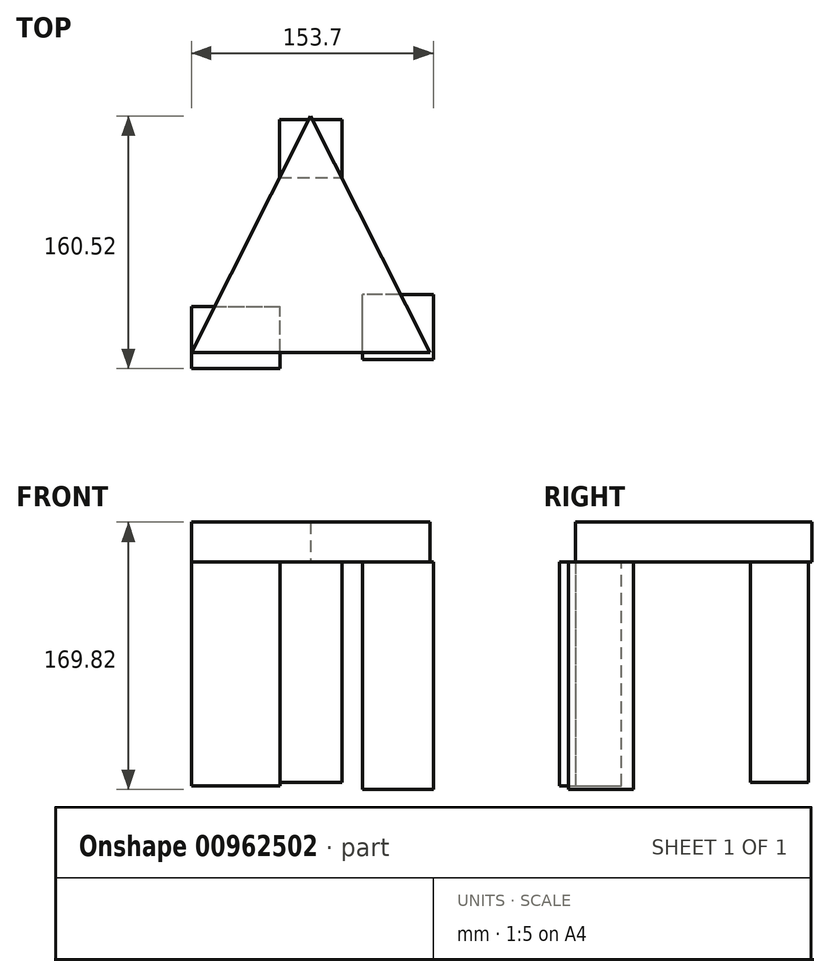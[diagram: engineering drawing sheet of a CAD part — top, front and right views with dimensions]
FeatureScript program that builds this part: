
annotation { "Feature Type Name" : "Feature", "Feature Type Description" : "" }
export const myFeature = defineFeature(function(context is Context, id is Id, definition is map)
    precondition{}
    {
        {
            var Q0;
            Q0=qCreatedBy(makeId("Top.planeOp"),FACE);
            var sketch = newSketch(context, id + "F0", { "sketchPlane" : qUnion([Q0])});
            skLineSegment(sketch, "E0", {"start": v(-13.9, 48.54) * mm, "end": v(-75.72, -75.51) * mm});
            skLineSegment(sketch, "E1", {"start": v(-75.72, -75.51) * mm, "end": v(0, 74.9) * mm});
            skLineSegment(sketch, "E2", {"start": v(75.72, -75.3) * mm, "end": v(0, 74.9) * mm});
            skLineSegment(sketch, "E3", {"start": v(75.72, -75.3) * mm, "end": v(-75.72, -75.51) * mm});
            skSolve(sketch);
        }
        {
            var Q0;
            Q0=makeQuery(id+"F0.imprint","IMPRINT",FACE,{"disambiguationData":[TD([[makeQuery(id+"F0.imprint","IMPRINT",EDGE,{"derivedFrom":sQuery(id+"F0.wireOp",EDGE,"E1")}),-1.0]])]});
            extrude(context, id + "F1", {"entities" : qUnion([Q0]), "depth" : 25.4 * mm, "offsetDistance" : 25.4 * mm});
        }
        {
            var Q0;
            Q0=makeQuery(id+"F1.opExtrude","CAP_FACE",FACE,{"disambiguationData":[OSD([sQuery(id+"F0.wireOp",EDGE,"E1"),sQuery(id+"F0.wireOp",EDGE,"E2"),sQuery(id+"F0.wireOp",EDGE,"E3")])],"isStart":true});
            var sketch = newSketch(context, id + "F2", { "sketchPlane" : qUnion([Q0])});
            skLineSegment(sketch, "E4.bottom", {"start": v(75.72, 75.3) * mm, "end": v(32.4, 75.3) * mm});
            skLineSegment(sketch, "E4.top", {"start": v(75.72, 43.67) * mm, "end": v(32.4, 43.67) * mm});
            skLineSegment(sketch, "E4.left", {"start": v(75.72, 75.3) * mm, "end": v(75.72, 43.67) * mm});
            skLineSegment(sketch, "E4.right", {"start": v(32.4, 75.3) * mm, "end": v(32.4, 43.67) * mm});
            skPoint(sketch, "E4.middle", {"position": v(54.06, 59.49) * mm});
            skLineSegment(sketch, "E5.bottom", {"start": v(-23.54, -28.13) * mm, "end": v(23.54, -28.13) * mm});
            skLineSegment(sketch, "E5.top", {"start": v(-23.54, -69.7) * mm, "end": v(23.54, -69.7) * mm});
            skLineSegment(sketch, "E5.left", {"start": v(-23.54, -28.13) * mm, "end": v(-23.54, -69.7) * mm});
            skLineSegment(sketch, "E5.right", {"start": v(23.54, -28.13) * mm, "end": v(23.54, -69.7) * mm});
            skPoint(sketch, "E5.middle", {"position": v(0, -48.92) * mm});
            skLineSegment(sketch, "E6.bottom", {"start": v(-85.45, 87) * mm, "end": v(-41.1, 87) * mm});
            skLineSegment(sketch, "E6.top", {"start": v(-85.45, 48.67) * mm, "end": v(-41.1, 48.67) * mm});
            skLineSegment(sketch, "E6.left", {"start": v(-85.45, 87) * mm, "end": v(-85.45, 48.67) * mm});
            skLineSegment(sketch, "E6.right", {"start": v(-41.1, 87) * mm, "end": v(-41.1, 48.67) * mm});
            skPoint(sketch, "E6.middle", {"position": v(-63.27, 67.84) * mm});
            skSolve(sketch);
        }
        {
            var Q0;
            Q0=makeQuery(id+"F1.opExtrude","CAP_FACE",FACE,{"disambiguationData":[OSD([sQuery(id+"F0.wireOp",EDGE,"E1"),sQuery(id+"F0.wireOp",EDGE,"E2"),sQuery(id+"F0.wireOp",EDGE,"E3")])],"isStart":true});
            var sketch = newSketch(context, id + "F3", { "sketchPlane" : qUnion([Q0])});
            skLineSegment(sketch, "E7.bottom", {"start": v(89.03, 89.1) * mm, "end": v(31.32, 89.1) * mm});
            skLineSegment(sketch, "E7.top", {"start": v(89.03, 31.83) * mm, "end": v(31.32, 31.83) * mm});
            skLineSegment(sketch, "E7.left", {"start": v(89.03, 89.1) * mm, "end": v(89.03, 31.83) * mm});
            skLineSegment(sketch, "E7.right", {"start": v(31.32, 89.1) * mm, "end": v(31.32, 31.83) * mm});
            skPoint(sketch, "E7.middle", {"position": v(60.17, 60.47) * mm});
            skSolve(sketch);
        }
        {
            var Q0;
            {var subQ0=sQuery(id+"F2.wireOp",EDGE,"E6.right");var subQ1=sQuery(id+"F2.wireOp",EDGE,"E6.top");var subQ2=makeQuery(id+"F2.imprint","INTERSECT",VERTEX,{"derivedFrom":[subQ1,subQ0]});Q0=makeQuery(id+"F2.imprint","IMPRINT",FACE,{"disambiguationData":[TD([[makeQuery(id+"F2.imprint","IMPRINT",EDGE,{"disambiguationData":[TD([[subQ2,1.0]])],"derivedFrom":subQ1}),1.0]])]});}
            var sketch = newSketch(context, id + "F4", { "sketchPlane" : qUnion([Q0])});
            skLineSegment(sketch, "E8.bottom", {"start": v(-75.55, 85.63) * mm, "end": v(-19.56, 85.63) * mm});
            skLineSegment(sketch, "E8.top", {"start": v(-75.55, 46.26) * mm, "end": v(-19.56, 46.26) * mm});
            skLineSegment(sketch, "E8.left", {"start": v(-75.55, 85.63) * mm, "end": v(-75.55, 46.26) * mm});
            skLineSegment(sketch, "E8.right", {"start": v(-19.56, 85.63) * mm, "end": v(-19.56, 46.26) * mm});
            skPoint(sketch, "E8.middle", {"position": v(-47.56, 65.95) * mm});
            skSolve(sketch);
        }
        {
            var Q0;
            {var subQ0=sQuery(id+"F2.wireOp",EDGE,"E6.right");var subQ1=sQuery(id+"F2.wireOp",EDGE,"E6.top");var subQ2=makeQuery(id+"F2.imprint","INTERSECT",VERTEX,{"derivedFrom":[subQ1,subQ0]});Q0=makeQuery(id+"F2.imprint","IMPRINT",FACE,{"disambiguationData":[TD([[makeQuery(id+"F2.imprint","IMPRINT",EDGE,{"disambiguationData":[TD([[subQ2,1.0]])],"derivedFrom":subQ1}),1.0]])]});}
            var Q1;
            Q1 = qSketchRegion(id + "F4", true);
            extrude(context, id + "F5", {"entities" : qUnion([Q0, Q1]), "operationType" : NewBodyOperationType.ADD, "depth" : 142.07 * mm, "offsetDistance" : 25.4 * mm});
        }
        {
            var Q0;
            Q0=makeQuery(id+"F1.opExtrude","CAP_FACE",FACE,{"disambiguationData":[OSD([sQuery(id+"F0.wireOp",EDGE,"E1"),sQuery(id+"F0.wireOp",EDGE,"E2"),sQuery(id+"F0.wireOp",EDGE,"E3")])],"isStart":true});
            var sketch = newSketch(context, id + "F6", { "sketchPlane" : qUnion([Q0])});
            skLineSegment(sketch, "E9.bottom", {"start": v(-19.84, -72.44) * mm, "end": v(19.84, -72.44) * mm});
            skLineSegment(sketch, "E9.top", {"start": v(-19.84, -35.89) * mm, "end": v(19.84, -35.89) * mm});
            skLineSegment(sketch, "E9.left", {"start": v(-19.84, -72.44) * mm, "end": v(-19.84, -35.89) * mm});
            skLineSegment(sketch, "E9.right", {"start": v(19.84, -72.44) * mm, "end": v(19.84, -35.89) * mm});
            skPoint(sketch, "E9.middle", {"position": v(0, -54.17) * mm});
            skSolve(sketch);
        }
        {
            var Q0;
            Q0 = qSketchRegion(id + "F6", true);
            extrude(context, id + "F7", {"entities" : qUnion([Q0]), "operationType" : NewBodyOperationType.ADD, "depth" : 139.84 * mm, "offsetDistance" : 25.4 * mm});
        }
        {
            var Q0;
            {var subQ0=sQuery(id+"F3.wireOp",EDGE,"E7.right");var subQ1=sQuery(id+"F3.wireOp",EDGE,"E7.top");var subQ2=makeQuery(id+"F3.imprint","INTERSECT",VERTEX,{"derivedFrom":[subQ1,subQ0]});Q0=makeQuery(id+"F3.imprint","IMPRINT",FACE,{"disambiguationData":[TD([[makeQuery(id+"F3.imprint","IMPRINT",EDGE,{"disambiguationData":[TD([[subQ2,1.0]])],"derivedFrom":subQ1}),-1.0]])]});}
            var sketch = newSketch(context, id + "F8", { "sketchPlane" : qUnion([Q0])});
            skLineSegment(sketch, "E10.bottom", {"start": v(77.98, 79.9) * mm, "end": v(32.96, 79.9) * mm});
            skLineSegment(sketch, "E10.top", {"start": v(77.98, 38.67) * mm, "end": v(32.96, 38.67) * mm});
            skLineSegment(sketch, "E10.left", {"start": v(77.98, 79.9) * mm, "end": v(77.98, 38.67) * mm});
            skLineSegment(sketch, "E10.right", {"start": v(32.96, 79.9) * mm, "end": v(32.96, 38.67) * mm});
            skPoint(sketch, "E10.middle", {"position": v(55.47, 59.29) * mm});
            skSolve(sketch);
        }
        {
            var Q0;
            Q0 = qSketchRegion(id + "F8", true);
            extrude(context, id + "F9", {"entities" : qUnion([Q0]), "operationType" : NewBodyOperationType.ADD, "depth" : 144.42 * mm, "offsetDistance" : 25.4 * mm});
        }
    });
